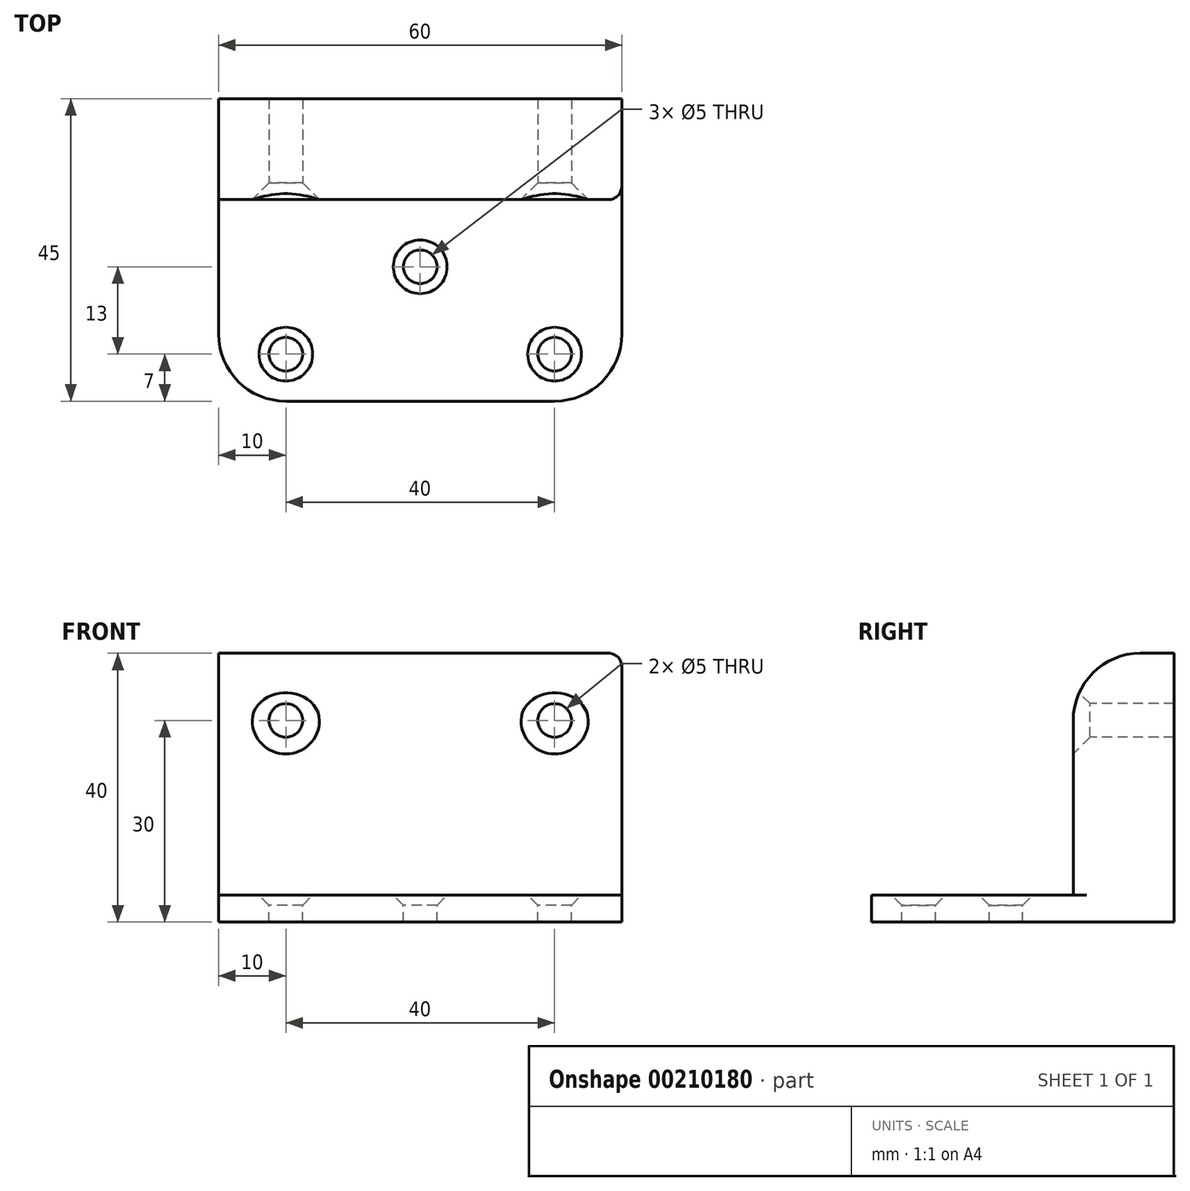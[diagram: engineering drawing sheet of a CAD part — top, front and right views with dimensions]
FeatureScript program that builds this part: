
annotation { "Feature Type Name" : "Feature", "Feature Type Description" : "" }
export const myFeature = defineFeature(function(context is Context, id is Id, definition is map)
    precondition{}
    {
        {
            var Q0;
            Q0=qCreatedBy(makeId("Top.planeOp"),FACE);
            var sketch = newSketch(context, id + "F0", { "sketchPlane" : qUnion([Q0])});
            skLineSegment(sketch, "E0.bottom", {"start": v(-30, 15) * mm, "end": v(30, 15) * mm});
            skLineSegment(sketch, "E0.top", {"start": v(-30, 0) * mm, "end": v(30, 0) * mm});
            skLineSegment(sketch, "E0.left", {"start": v(-30, 15) * mm, "end": v(-30, 0) * mm});
            skLineSegment(sketch, "E0.right", {"start": v(30, 15) * mm, "end": v(30, 0) * mm});
            skLineSegment(sketch, "E1.top", {"start": v(-30, -30) * mm, "end": v(30, -30) * mm});
            skLineSegment(sketch, "E1.left", {"start": v(-30, 0) * mm, "end": v(-30, -30) * mm});
            skLineSegment(sketch, "E1.right", {"start": v(30, 0) * mm, "end": v(30, -30) * mm});
            skSolve(sketch);
        }
        {
            var Q0;
            Q0=makeQuery(id+"F0.imprint","IMPRINT",FACE,{"disambiguationData":[TD([[makeQuery(id+"F0.imprint","IMPRINT",EDGE,{"derivedFrom":sQuery(id+"F0.wireOp",EDGE,"E0.bottom")}),-1.0]])]});
            extrude(context, id + "F1", {"entities" : qUnion([Q0]), "depth" : 40 * mm});
        }
        {
            var Q0;
            Q0=makeQuery(id+"F0.imprint","IMPRINT",FACE,{"disambiguationData":[TD([[makeQuery(id+"F0.imprint","IMPRINT",EDGE,{"derivedFrom":sQuery(id+"F0.wireOp",EDGE,"E0.top")}),-1.0]])]});
            extrude(context, id + "F2", {"entities" : qUnion([Q0]), "operationType" : NewBodyOperationType.ADD, "depth" : 4 * mm});
        }
        {
            var Q0;
            Q0=makeQuery(id+"F1.opExtrude","SWEPT_FACE",FACE,{"disambiguationData":[OSD([sQuery(id+"F0.wireOp",EDGE,"E0.top"),sQuery(id+"F0.wireOp",EDGE,"E0.top")])]});
            var sketch = newSketch(context, id + "F3", { "sketchPlane" : qUnion([Q0])});
            skPoint(sketch, "E2", {"position": v(-20, 30) * mm});
            skPoint(sketch, "E3", {"position": v(20, 30) * mm});
            skSolve(sketch);
        }
        {
            var Q0;
            Q0=sQuery(id+"F3.wireOp",VERTEX,"E2");
            var Q1;
            Q1=sQuery(id+"F3.wireOp",VERTEX,"E3");
            var Q2;
            Q2=makeQuery(id+"F1.opExtrude","SWEPT_BODY",BODY,{"disambiguationData":[OSD([sQuery(id+"F0.wireOp",EDGE,"E0.bottom"),sQuery(id+"F0.wireOp",EDGE,"E0.top"),sQuery(id+"F0.wireOp",EDGE,"E0.left"),sQuery(id+"F0.wireOp",EDGE,"E0.right"),sQuery(id+"F0.wireOp",EDGE,"E0.top")])]});
            hole(context, id + "F4", {"style" : HoleStyle.C_SINK, "endStyle" : HoleEndStyle.THROUGH, "holeDiameter" : 5 * mm, "cSinkDiameter" : 10 * mm, "cSinkAngle" : 90 * degree, "locations" : qUnion([Q0, Q1]), "scope" : qUnion([Q2]), "tappedDepth" : 12 * mm, "tapClearance" : 3});
        }
        {
            var Q0;
            Q0=makeQuery(id+"F2.opExtrude","CAP_FACE",FACE,{"disambiguationData":[OSD([sQuery(id+"F0.wireOp",EDGE,"E0.top"),sQuery(id+"F0.wireOp",EDGE,"E1.top"),sQuery(id+"F0.wireOp",EDGE,"E1.left"),sQuery(id+"F0.wireOp",EDGE,"E1.right")])],"isStart":false});
            var sketch = newSketch(context, id + "F5", { "sketchPlane" : qUnion([Q0])});
            skPoint(sketch, "E4", {"position": v(0, -10) * mm});
            skPoint(sketch, "E5", {"position": v(-20, -23) * mm});
            skPoint(sketch, "E6", {"position": v(20, -23) * mm});
            skSolve(sketch);
        }
        {
            var Q0;
            Q0=sQuery(id+"F5.wireOp",VERTEX,"E4");
            var Q1;
            Q1=sQuery(id+"F5.wireOp",VERTEX,"E5");
            var Q2;
            Q2=sQuery(id+"F5.wireOp",VERTEX,"E6");
            var Q3;
            Q3=makeQuery(id+"F1.opExtrude","SWEPT_BODY",BODY,{"disambiguationData":[OSD([sQuery(id+"F0.wireOp",EDGE,"E0.bottom"),sQuery(id+"F0.wireOp",EDGE,"E0.top"),sQuery(id+"F0.wireOp",EDGE,"E0.left"),sQuery(id+"F0.wireOp",EDGE,"E0.right"),sQuery(id+"F0.wireOp",EDGE,"E0.top")])]});
            hole(context, id + "F6", {"style" : HoleStyle.C_SINK, "endStyle" : HoleEndStyle.THROUGH, "holeDiameter" : 5 * mm, "cSinkDiameter" : 8 * mm, "cSinkAngle" : 90 * degree, "locations" : qUnion([Q0, Q1, Q2]), "scope" : qUnion([Q3]), "tappedDepth" : 12 * mm, "tapClearance" : 3});
        }
        {
            var Q0;
            Q0=makeQuery(id+"F2.opExtrude","CAP_EDGE",EDGE,{"disambiguationData":[OSD([sQuery(id+"F0.wireOp",EDGE,"E0.top")])],"isStart":false});
            var Q1;
            Q1=makeQuery(id+"F2.opExtrude","SWEPT_EDGE",EDGE,{"disambiguationData":[OSD([sQuery(id+"F0.wireOp",EDGE,"E0.top"),sQuery(id+"F0.wireOp",EDGE,"E0.top"),sQuery(id+"F0.wireOp",EDGE,"E1.left")])]});
            var Q2;
            Q2=makeQuery(id+"F2.opExtrude","SWEPT_EDGE",EDGE,{"disambiguationData":[OSD([sQuery(id+"F0.wireOp",EDGE,"E0.top"),sQuery(id+"F0.wireOp",EDGE,"E0.top"),sQuery(id+"F0.wireOp",EDGE,"E1.right")])]});
            var Q3;
            Q3=makeQuery(id+"F2.opExtrude","SWEPT_EDGE",EDGE,{"disambiguationData":[OSD([sQuery(id+"F0.wireOp",EDGE,"E1.top"),sQuery(id+"F0.wireOp",EDGE,"E1.right")])]});
            var Q4;
            Q4=makeQuery(id+"F2.opExtrude","SWEPT_EDGE",EDGE,{"disambiguationData":[OSD([sQuery(id+"F0.wireOp",EDGE,"E1.top"),sQuery(id+"F0.wireOp",EDGE,"E1.left")])]});
            fillet(context, id + "F7", {"entities" : qUnion([Q0, Q1, Q2, Q3, Q4]), "radius" : 10 * mm, "tangentPropagation" : true, "allowEdgeOverflow" : false});
        }
        {
            var Q0;
            Q0=makeQuery(id+"F7.opFillet","BLEND_EDGE",EDGE,{"blendedFrom":[makeQuery(id+"F2.opExtrude","SWEPT_EDGE",EDGE,{"disambiguationData":[OSD([sQuery(id+"F0.wireOp",EDGE,"E0.top"),sQuery(id+"F0.wireOp",EDGE,"E0.top"),sQuery(id+"F0.wireOp",EDGE,"E1.left")])]}),makeQuery(id+"F1.opExtrude","SWEPT_FACE",FACE,{"disambiguationData":[OSD([sQuery(id+"F0.wireOp",EDGE,"E0.left")])]})],"blendedInto":[makeQuery(id+"F1.opExtrude","SWEPT_FACE",FACE,{"disambiguationData":[OSD([sQuery(id+"F0.wireOp",EDGE,"E0.left")])]})]});
            var Q1;
            Q1=makeQuery(id+"F7.opFillet","BLEND_EDGE",EDGE,{"blendedFrom":[makeQuery(id+"F2.opExtrude","SWEPT_EDGE",EDGE,{"disambiguationData":[OSD([sQuery(id+"F0.wireOp",EDGE,"E0.top"),sQuery(id+"F0.wireOp",EDGE,"E0.top"),sQuery(id+"F0.wireOp",EDGE,"E1.right")])]}),makeQuery(id+"F1.opExtrude","SWEPT_FACE",FACE,{"disambiguationData":[OSD([sQuery(id+"F0.wireOp",EDGE,"E0.right")])]})],"blendedInto":[makeQuery(id+"F1.opExtrude","SWEPT_FACE",FACE,{"disambiguationData":[OSD([sQuery(id+"F0.wireOp",EDGE,"E0.right")])]})]});
            var Q2;
            Q2=makeQuery(id+"F1.opExtrude","CAP_EDGE",EDGE,{"disambiguationData":[OSD([sQuery(id+"F0.wireOp",EDGE,"E0.top"),sQuery(id+"F0.wireOp",EDGE,"E0.top")])],"isStart":false});
            fillet(context, id + "F8", {"entities" : qUnion([Q0, Q1, Q2]), "radius" : 10 * mm, "tangentPropagation" : true, "allowEdgeOverflow" : false});
        }
        {
            var Q0;
            Q0=makeQuery(id+"F1.opExtrude","SWEPT_EDGE",EDGE,{"disambiguationData":[OSD([sQuery(id+"F0.wireOp",EDGE,"E0.right"),sQuery(id+"F0.wireOp",EDGE,"E0.top"),sQuery(id+"F0.wireOp",EDGE,"E1.right")])]});
            fillet(context, id + "F9", {"entities" : qUnion([Q0]), "radius" : 2 * mm, "tangentPropagation" : true, "allowEdgeOverflow" : false});
        }
    });
